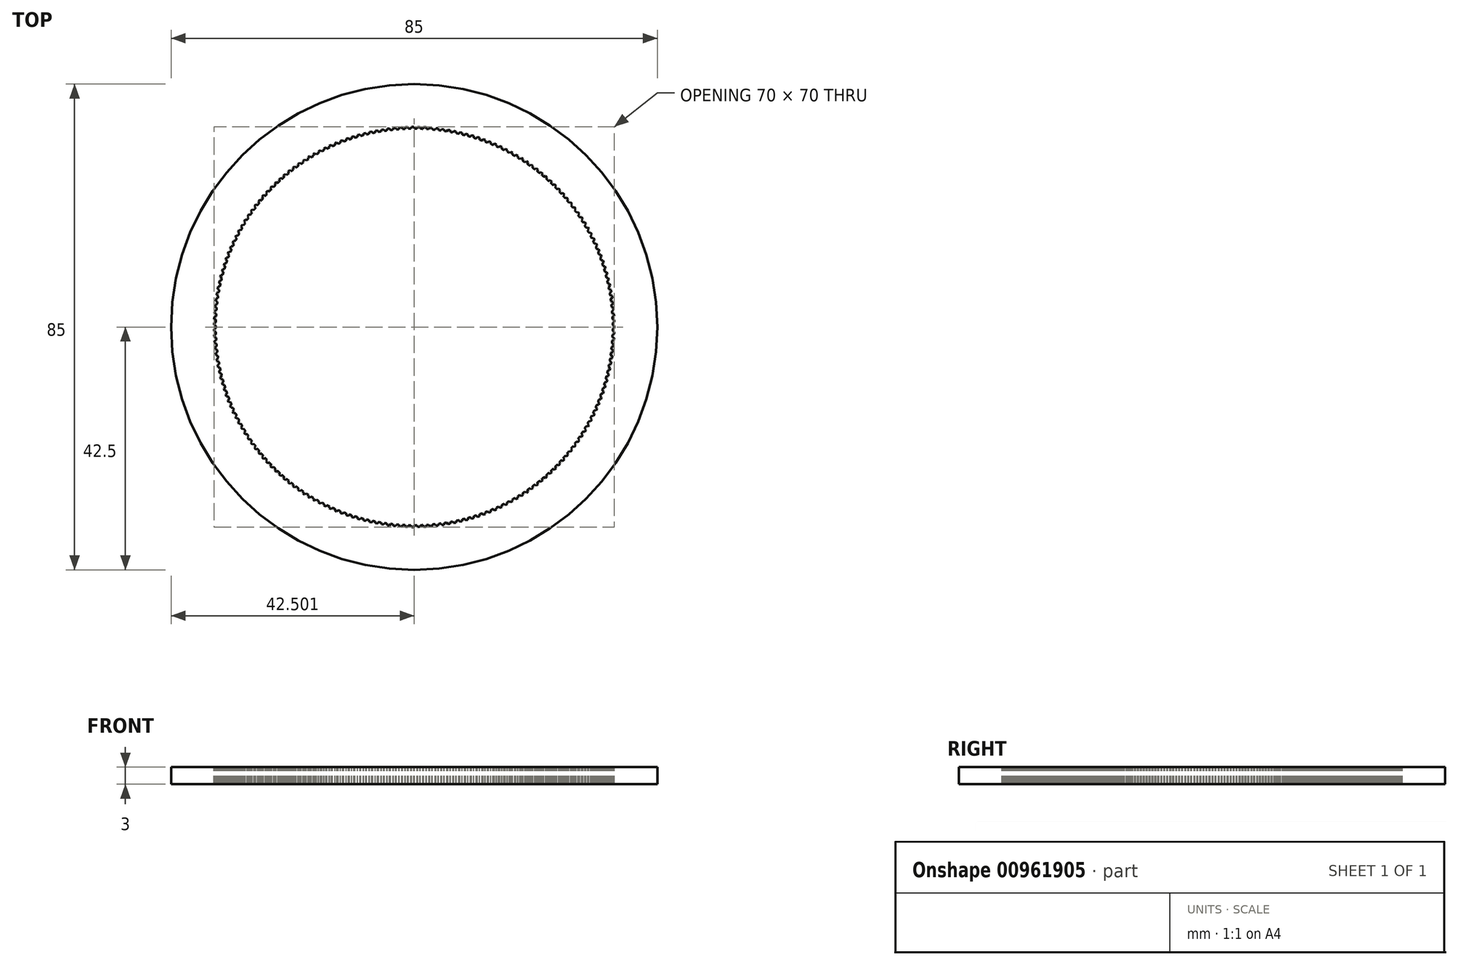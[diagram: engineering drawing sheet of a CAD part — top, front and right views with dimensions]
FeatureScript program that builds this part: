
annotation { "Feature Type Name" : "Feature", "Feature Type Description" : "" }
export const myFeature = defineFeature(function(context is Context, id is Id, definition is map)
    precondition{}
    {
        {
            assignVariable(context, id + "F0", {"name" : "ID", "anyValue" : 69.4});
        }
        {
            assignVariable(context, id + "F1", {"name" : "IW", "anyValue" : 0.6});
        }
        {
            assignVariable(context, id + "F2", {"name" : "GD", "anyValue" : 3});
        }
        {
            var Q0;
            Q0=qCreatedBy(makeId("Top.planeOp"),FACE);
            var sketch = newSketch(context, id + "F3", { "sketchPlane" : qUnion([Q0])});
            skCircle(sketch, "E0", {"center": v(0, 0) * mm, "radius": 34.7 * mm});
            skSolve(sketch);
        }
        {
            var Q0;
            Q0=qSketchRegion(id+"F3",true);
            extrude(context, id + "F4", {"entities" : qUnion([Q0]), "depth" : (getVariable(context, 'GD')) * mm, "offsetDistance" : 25 * mm});
        }
        {
            var Q0;
            Q0=makeQuery(id+"F4.opExtrude","CAP_FACE",FACE,{"disambiguationData":[OSD([sQuery(id+"F3.wireOp",EDGE,"E0")])],"isStart":false});
            var sketch = newSketch(context, id + "F5", { "sketchPlane" : qUnion([Q0])});
            skLineSegment(sketch, "E1", {"start": v(0, 0) * mm, "end": v(14.18, 0) * mm, "construction": true});
            skLineSegment(sketch, "E2", {"start": v(35, 0.2) * mm, "end": v(35, -0.2) * mm});
            skLineSegment(sketch, "E3", {"start": v(35, -0.2) * mm, "end": v(34.7, -0.3) * mm});
            skLineSegment(sketch, "E4", {"start": v(34.7, -0.3) * mm, "end": v(34.7, 0.3) * mm, "construction": true});
            skLineSegment(sketch, "E5", {"start": v(34.7, 0.3) * mm, "end": v(35, 0.2) * mm});
            skLineSegment(sketch, "E6", {"start": v(34.7, 0.3) * mm, "end": v(34.6, 0.3) * mm});
            skLineSegment(sketch, "E7", {"start": v(34.6, 0.3) * mm, "end": v(34.6, -0.3) * mm});
            skLineSegment(sketch, "E8", {"start": v(34.6, -0.3) * mm, "end": v(34.7, -0.3) * mm});
            skSolve(sketch);
        }
        {
            assignVariable(context, id + "F6", {"name" : "TM1", "anyValue" : 3.14 * 2 * getVariable(context, 'ID')});
        }
        {
            assignVariable(context, id + "F7", {"name" : "NoT", "anyValue" : floor((getVariable(context, 'TM1')) / (3.5 * getVariable(context, 'IW')))});
        }
        {
            var Q0;
            Q0=qSketchRegion(id+"F5",true);
            extrude(context, id + "F8", {"entities" : qUnion([Q0]), "oppositeDirection" : true, "depth" : (getVariable(context, 'GD')) * mm, "offsetDistance" : 25 * mm});
        }
        {
            var Q0;
            Q0=makeQuery(id+"F8.opExtrude","SWEPT_BODY",BODY,{"disambiguationData":[OSD([sQuery(id+"F5.wireOp",EDGE,"E2"),sQuery(id+"F5.wireOp",EDGE,"E3"),sQuery(id+"F5.wireOp",EDGE,"E5"),sQuery(id+"F5.wireOp",EDGE,"E6"),sQuery(id+"F5.wireOp",EDGE,"E7"),sQuery(id+"F5.wireOp",EDGE,"E8")])]});
            var Q1;
            Q1=makeQuery(id+"F4.opExtrude","SWEPT_FACE",FACE,{"disambiguationData":[OSD([sQuery(id+"F3.wireOp",EDGE,"E0")])]});
            circularPattern(context, id + "F9", {"operationType" : NewBodyOperationType.ADD, "entities" : qUnion([Q0]), "axis" : qUnion([Q1]), "angle" : 360 * degree, "instanceCount" : getVariable(context, 'NoT'), "equalSpace" : true});
        }
        {
            var Q0;
            {var subQ0=makeQuery(id+"F8.opExtrude","CAP_FACE",FACE,{"disambiguationData":[OSD([sQuery(id+"F5.wireOp",EDGE,"E2"),sQuery(id+"F5.wireOp",EDGE,"E3"),sQuery(id+"F5.wireOp",EDGE,"E5"),sQuery(id+"F5.wireOp",EDGE,"E6"),sQuery(id+"F5.wireOp",EDGE,"E7"),sQuery(id+"F5.wireOp",EDGE,"E8")])],"isStart":false});Q0=makeQuery(id+"F9.boolean.opBoolean","MERGE",FACE,{"derivedFrom":[makeQuery(id+"F4.opExtrude","CAP_FACE",FACE,{"disambiguationData":[OSD([sQuery(id+"F3.wireOp",EDGE,"E0")])],"isStart":true}),subQ0,makeQuery(id+"F9.opPattern","COPY",FACE,{"derivedFrom":subQ0,"instanceName":"1"}),makeQuery(id+"F9.opPattern","COPY",FACE,{"derivedFrom":subQ0,"instanceName":"2"}),makeQuery(id+"F9.opPattern","COPY",FACE,{"derivedFrom":subQ0,"instanceName":"3"}),makeQuery(id+"F9.opPattern","COPY",FACE,{"derivedFrom":subQ0,"instanceName":"4"}),makeQuery(id+"F9.opPattern","COPY",FACE,{"derivedFrom":subQ0,"instanceName":"5"}),makeQuery(id+"F9.opPattern","COPY",FACE,{"derivedFrom":subQ0,"instanceName":"6"}),makeQuery(id+"F9.opPattern","COPY",FACE,{"derivedFrom":subQ0,"instanceName":"7"}),makeQuery(id+"F9.opPattern","COPY",FACE,{"derivedFrom":subQ0,"instanceName":"8"}),makeQuery(id+"F9.opPattern","COPY",FACE,{"derivedFrom":subQ0,"instanceName":"9"}),makeQuery(id+"F9.opPattern","COPY",FACE,{"derivedFrom":subQ0,"instanceName":"10"}),makeQuery(id+"F9.opPattern","COPY",FACE,{"derivedFrom":subQ0,"instanceName":"11"}),makeQuery(id+"F9.opPattern","COPY",FACE,{"derivedFrom":subQ0,"instanceName":"12"}),makeQuery(id+"F9.opPattern","COPY",FACE,{"derivedFrom":subQ0,"instanceName":"13"}),makeQuery(id+"F9.opPattern","COPY",FACE,{"derivedFrom":subQ0,"instanceName":"14"}),makeQuery(id+"F9.opPattern","COPY",FACE,{"derivedFrom":subQ0,"instanceName":"15"}),makeQuery(id+"F9.opPattern","COPY",FACE,{"derivedFrom":subQ0,"instanceName":"16"}),makeQuery(id+"F9.opPattern","COPY",FACE,{"derivedFrom":subQ0,"instanceName":"17"}),makeQuery(id+"F9.opPattern","COPY",FACE,{"derivedFrom":subQ0,"instanceName":"18"}),makeQuery(id+"F9.opPattern","COPY",FACE,{"derivedFrom":subQ0,"instanceName":"19"}),makeQuery(id+"F9.opPattern","COPY",FACE,{"derivedFrom":subQ0,"instanceName":"20"}),makeQuery(id+"F9.opPattern","COPY",FACE,{"derivedFrom":subQ0,"instanceName":"21"}),makeQuery(id+"F9.opPattern","COPY",FACE,{"derivedFrom":subQ0,"instanceName":"22"}),makeQuery(id+"F9.opPattern","COPY",FACE,{"derivedFrom":subQ0,"instanceName":"23"}),makeQuery(id+"F9.opPattern","COPY",FACE,{"derivedFrom":subQ0,"instanceName":"24"}),makeQuery(id+"F9.opPattern","COPY",FACE,{"derivedFrom":subQ0,"instanceName":"25"}),makeQuery(id+"F9.opPattern","COPY",FACE,{"derivedFrom":subQ0,"instanceName":"26"}),makeQuery(id+"F9.opPattern","COPY",FACE,{"derivedFrom":subQ0,"instanceName":"27"}),makeQuery(id+"F9.opPattern","COPY",FACE,{"derivedFrom":subQ0,"instanceName":"28"}),makeQuery(id+"F9.opPattern","COPY",FACE,{"derivedFrom":subQ0,"instanceName":"29"}),makeQuery(id+"F9.opPattern","COPY",FACE,{"derivedFrom":subQ0,"instanceName":"30"}),makeQuery(id+"F9.opPattern","COPY",FACE,{"derivedFrom":subQ0,"instanceName":"31"}),makeQuery(id+"F9.opPattern","COPY",FACE,{"derivedFrom":subQ0,"instanceName":"32"}),makeQuery(id+"F9.opPattern","COPY",FACE,{"derivedFrom":subQ0,"instanceName":"33"}),makeQuery(id+"F9.opPattern","COPY",FACE,{"derivedFrom":subQ0,"instanceName":"34"}),makeQuery(id+"F9.opPattern","COPY",FACE,{"derivedFrom":subQ0,"instanceName":"35"}),makeQuery(id+"F9.opPattern","COPY",FACE,{"derivedFrom":subQ0,"instanceName":"36"}),makeQuery(id+"F9.opPattern","COPY",FACE,{"derivedFrom":subQ0,"instanceName":"37"}),makeQuery(id+"F9.opPattern","COPY",FACE,{"derivedFrom":subQ0,"instanceName":"38"}),makeQuery(id+"F9.opPattern","COPY",FACE,{"derivedFrom":subQ0,"instanceName":"39"}),makeQuery(id+"F9.opPattern","COPY",FACE,{"derivedFrom":subQ0,"instanceName":"40"}),makeQuery(id+"F9.opPattern","COPY",FACE,{"derivedFrom":subQ0,"instanceName":"41"}),makeQuery(id+"F9.opPattern","COPY",FACE,{"derivedFrom":subQ0,"instanceName":"42"}),makeQuery(id+"F9.opPattern","COPY",FACE,{"derivedFrom":subQ0,"instanceName":"43"})]});}
            var sketch = newSketch(context, id + "F10", { "sketchPlane" : qUnion([Q0])});
            skCircle(sketch, "E9", {"center": v(0, 0) * mm, "radius": 0.5 * mm});
            skSolve(sketch);
        }
        {
            var Q0;
            Q0=makeQuery(id+"F10.imprint","IMPRINT",FACE,{"disambiguationData":[TD([[makeQuery(id+"F10.imprint","IMPRINT",EDGE,{"derivedFrom":sQuery(id+"F10.wireOp",EDGE,"E9")}),1.0]])]});
            var Q1;
            {var subQ0=makeQuery(id+"F8.opExtrude","CAP_FACE",FACE,{"disambiguationData":[OSD([sQuery(id+"F5.wireOp",EDGE,"E2"),sQuery(id+"F5.wireOp",EDGE,"E3"),sQuery(id+"F5.wireOp",EDGE,"E5"),sQuery(id+"F5.wireOp",EDGE,"E6"),sQuery(id+"F5.wireOp",EDGE,"E7"),sQuery(id+"F5.wireOp",EDGE,"E8")])],"isStart":true});Q1=makeQuery(id+"F9.boolean.opBoolean","MERGE",FACE,{"derivedFrom":[makeQuery(id+"F4.opExtrude","CAP_FACE",FACE,{"disambiguationData":[OSD([sQuery(id+"F3.wireOp",EDGE,"E0")])],"isStart":false}),subQ0,makeQuery(id+"F9.opPattern","COPY",FACE,{"derivedFrom":subQ0,"instanceName":"1"}),makeQuery(id+"F9.opPattern","COPY",FACE,{"derivedFrom":subQ0,"instanceName":"2"}),makeQuery(id+"F9.opPattern","COPY",FACE,{"derivedFrom":subQ0,"instanceName":"3"}),makeQuery(id+"F9.opPattern","COPY",FACE,{"derivedFrom":subQ0,"instanceName":"4"}),makeQuery(id+"F9.opPattern","COPY",FACE,{"derivedFrom":subQ0,"instanceName":"5"}),makeQuery(id+"F9.opPattern","COPY",FACE,{"derivedFrom":subQ0,"instanceName":"6"}),makeQuery(id+"F9.opPattern","COPY",FACE,{"derivedFrom":subQ0,"instanceName":"7"}),makeQuery(id+"F9.opPattern","COPY",FACE,{"derivedFrom":subQ0,"instanceName":"8"}),makeQuery(id+"F9.opPattern","COPY",FACE,{"derivedFrom":subQ0,"instanceName":"9"}),makeQuery(id+"F9.opPattern","COPY",FACE,{"derivedFrom":subQ0,"instanceName":"10"}),makeQuery(id+"F9.opPattern","COPY",FACE,{"derivedFrom":subQ0,"instanceName":"11"}),makeQuery(id+"F9.opPattern","COPY",FACE,{"derivedFrom":subQ0,"instanceName":"12"}),makeQuery(id+"F9.opPattern","COPY",FACE,{"derivedFrom":subQ0,"instanceName":"13"}),makeQuery(id+"F9.opPattern","COPY",FACE,{"derivedFrom":subQ0,"instanceName":"14"}),makeQuery(id+"F9.opPattern","COPY",FACE,{"derivedFrom":subQ0,"instanceName":"15"}),makeQuery(id+"F9.opPattern","COPY",FACE,{"derivedFrom":subQ0,"instanceName":"16"}),makeQuery(id+"F9.opPattern","COPY",FACE,{"derivedFrom":subQ0,"instanceName":"17"}),makeQuery(id+"F9.opPattern","COPY",FACE,{"derivedFrom":subQ0,"instanceName":"18"}),makeQuery(id+"F9.opPattern","COPY",FACE,{"derivedFrom":subQ0,"instanceName":"19"}),makeQuery(id+"F9.opPattern","COPY",FACE,{"derivedFrom":subQ0,"instanceName":"20"}),makeQuery(id+"F9.opPattern","COPY",FACE,{"derivedFrom":subQ0,"instanceName":"21"}),makeQuery(id+"F9.opPattern","COPY",FACE,{"derivedFrom":subQ0,"instanceName":"22"}),makeQuery(id+"F9.opPattern","COPY",FACE,{"derivedFrom":subQ0,"instanceName":"23"}),makeQuery(id+"F9.opPattern","COPY",FACE,{"derivedFrom":subQ0,"instanceName":"24"}),makeQuery(id+"F9.opPattern","COPY",FACE,{"derivedFrom":subQ0,"instanceName":"25"}),makeQuery(id+"F9.opPattern","COPY",FACE,{"derivedFrom":subQ0,"instanceName":"26"}),makeQuery(id+"F9.opPattern","COPY",FACE,{"derivedFrom":subQ0,"instanceName":"27"}),makeQuery(id+"F9.opPattern","COPY",FACE,{"derivedFrom":subQ0,"instanceName":"28"}),makeQuery(id+"F9.opPattern","COPY",FACE,{"derivedFrom":subQ0,"instanceName":"29"}),makeQuery(id+"F9.opPattern","COPY",FACE,{"derivedFrom":subQ0,"instanceName":"30"}),makeQuery(id+"F9.opPattern","COPY",FACE,{"derivedFrom":subQ0,"instanceName":"31"}),makeQuery(id+"F9.opPattern","COPY",FACE,{"derivedFrom":subQ0,"instanceName":"32"}),makeQuery(id+"F9.opPattern","COPY",FACE,{"derivedFrom":subQ0,"instanceName":"33"}),makeQuery(id+"F9.opPattern","COPY",FACE,{"derivedFrom":subQ0,"instanceName":"34"}),makeQuery(id+"F9.opPattern","COPY",FACE,{"derivedFrom":subQ0,"instanceName":"35"}),makeQuery(id+"F9.opPattern","COPY",FACE,{"derivedFrom":subQ0,"instanceName":"36"}),makeQuery(id+"F9.opPattern","COPY",FACE,{"derivedFrom":subQ0,"instanceName":"37"}),makeQuery(id+"F9.opPattern","COPY",FACE,{"derivedFrom":subQ0,"instanceName":"38"}),makeQuery(id+"F9.opPattern","COPY",FACE,{"derivedFrom":subQ0,"instanceName":"39"}),makeQuery(id+"F9.opPattern","COPY",FACE,{"derivedFrom":subQ0,"instanceName":"40"}),makeQuery(id+"F9.opPattern","COPY",FACE,{"derivedFrom":subQ0,"instanceName":"41"}),makeQuery(id+"F9.opPattern","COPY",FACE,{"derivedFrom":subQ0,"instanceName":"42"}),makeQuery(id+"F9.opPattern","COPY",FACE,{"derivedFrom":subQ0,"instanceName":"43"})]});}
            extrude(context, id + "F11", {"entities" : qUnion([Q0]), "operationType" : NewBodyOperationType.REMOVE, "endBound" : BoundingType.UP_TO_SURFACE, "oppositeDirection" : true, "depth" : 25 * mm, "endBoundEntityFace" : qUnion([Q1]), "offsetDistance" : 25 * mm});
        }
        {
            var Q0;
            Q0=qCreatedBy(makeId("Top.planeOp"),FACE);
            var sketch = newSketch(context, id + "F12", { "sketchPlane" : qUnion([Q0])});
            skCircle(sketch, "E10", {"center": v(0, 0) * mm, "radius": 42.5 * mm});
            skSolve(sketch);
        }
        {
            var Q0;
            Q0 = qSketchRegion(id + "F12", true);
            extrude(context, id + "F13", {"entities" : qUnion([Q0]), "depth" : 3 * mm, "offsetDistance" : 25 * mm});
        }
        {
            var Q0;
            Q0=makeQuery(id+"F4.opExtrude","SWEPT_BODY",BODY,{"disambiguationData":[OSD([sQuery(id+"F3.wireOp",EDGE,"E0")])]});
            var Q1;
            Q1=makeQuery(id+"F13.opExtrude","SWEPT_BODY",BODY,{"disambiguationData":[OSD([sQuery(id+"F12.wireOp",EDGE,"E10")])]});
            booleanBodies(context, id + "F14", {"operationType" : BooleanOperationType.SUBTRACTION, "tools" : qUnion([Q0]), "targets" : qUnion([Q1])});
        }
        {
            var Q0;
            Q0=makeQuery(id+"F14.opBoolean","SPLIT",FACE,{"disambiguationData":[TD([makeQuery(id+"F11.boolean.opBoolean","COPY",FACE,{"derivedFrom":makeQuery(id+"F11.opExtrude","SWEPT_FACE",FACE,{"disambiguationData":[OSD([sQuery(id+"F10.wireOp",EDGE,"E9")])]})})])],"derivedFrom":makeQuery(id+"F13.opExtrude","CAP_FACE",FACE,{"disambiguationData":[OSD([sQuery(id+"F12.wireOp",EDGE,"E10")])],"isStart":false})});
            extrude(context, id + "F15", {"entities" : qUnion([Q0]), "operationType" : NewBodyOperationType.REMOVE, "oppositeDirection" : true, "depth" : 25 * mm, "offsetDistance" : 25 * mm});
        }
    });
